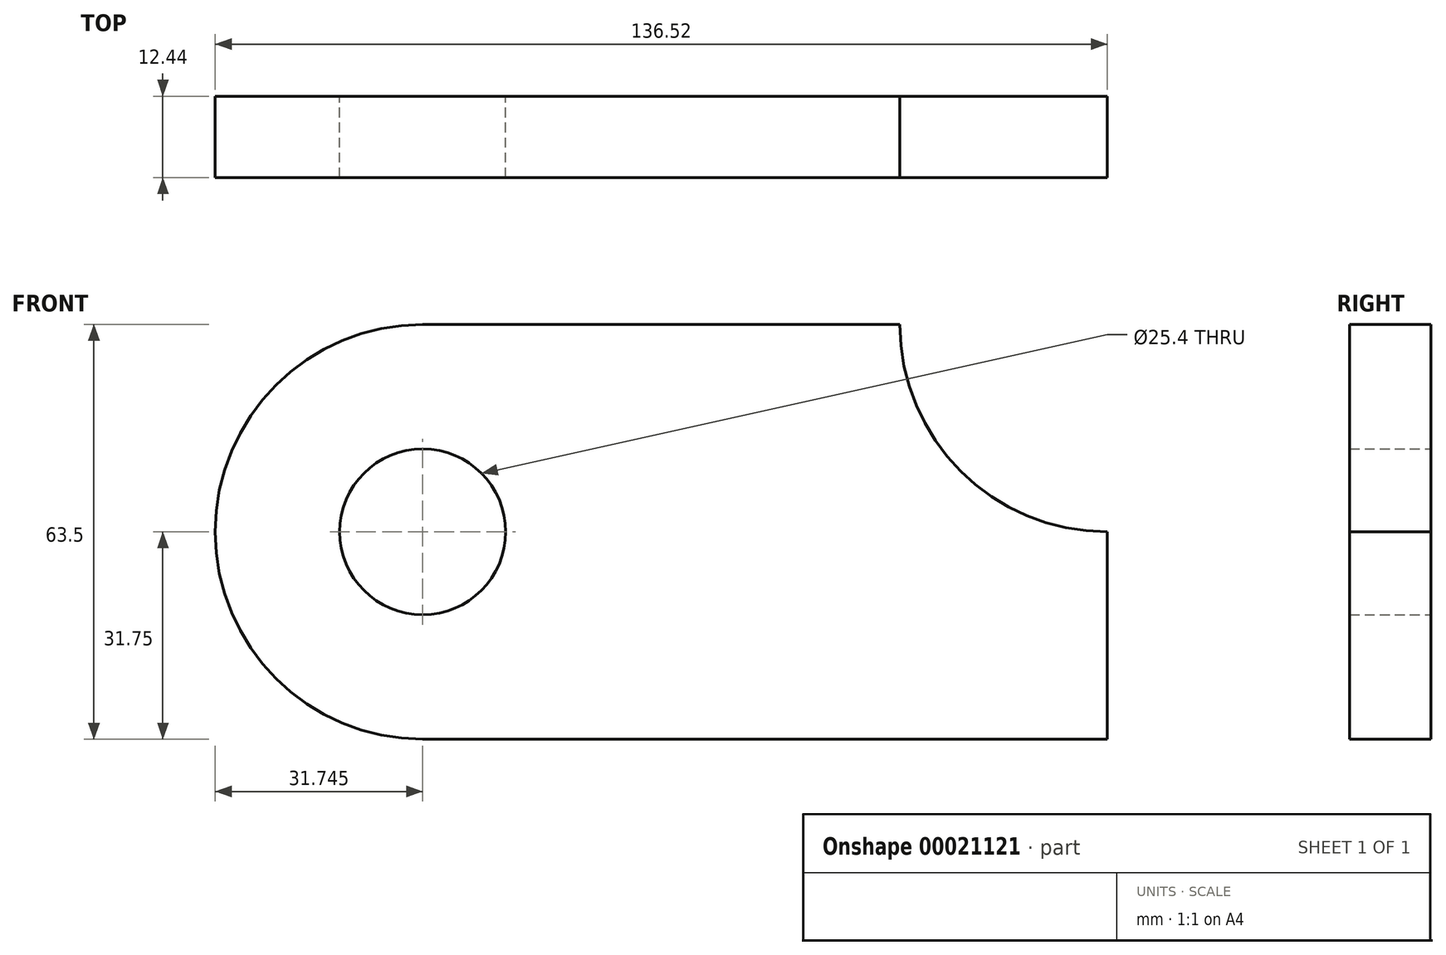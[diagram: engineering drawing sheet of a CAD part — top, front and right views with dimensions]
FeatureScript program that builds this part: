
annotation { "Feature Type Name" : "Feature", "Feature Type Description" : "" }
export const myFeature = defineFeature(function(context is Context, id is Id, definition is map)
    precondition{}
    {
        {
            var Q0;
            Q0=qCreatedBy(makeId("Front.planeOp"),FACE);
            var sketch = newSketch(context, id + "F0", { "sketchPlane" : qUnion([Q0])});
            skLineSegment(sketch, "E0.bottom", {"start": v(0, 0) * mm, "end": v(-104.78, 0) * mm});
            skLineSegment(sketch, "E0.top", {"start": v(0, 63.5) * mm, "end": v(-104.77, 63.5) * mm});
            skLineSegment(sketch, "E0.left", {"start": v(0, 0) * mm, "end": v(0, 63.5) * mm});
            skLineSegment(sketch, "E0.right", {"start": v(-104.78, 0) * mm, "end": v(-104.77, 63.5) * mm});
            skCircle(sketch, "E1", {"center": v(-104.77, 31.75) * mm, "radius": 31.75 * mm});
            skCircle(sketch, "E2", {"center": v(-104.77, 31.75) * mm, "radius": 12.7 * mm});
            skCircle(sketch, "E3", {"center": v(0, 63.5) * mm, "radius": 31.75 * mm});
            skSolve(sketch);
        }
        {
            var Q0;
            {var subQ4=sQuery(id+"F0.wireOp",EDGE,"E0.bottom");Q0=makeQuery(id+"F0.imprint","IMPRINT",FACE,{"disambiguationData":[TD([[makeQuery(id+"F0.imprint","IMPRINT",EDGE,{"derivedFrom":subQ4}),-1.0]])]});}
            var Q1;
            {var subQ0=sQuery(id+"F0.wireOp",EDGE,"E2");var subQ1=sQuery(id+"F0.wireOp",EDGE,"E0.right");var subQ3=makeQuery(id+"F0.imprint","INTERSECT",VERTEX,{"disambiguationData":[OD(0.0)],"derivedFrom":[subQ1,subQ0]});Q1=makeQuery(id+"F0.imprint","IMPRINT",FACE,{"disambiguationData":[TD([[makeQuery(id+"F0.imprint","IMPRINT",EDGE,{"disambiguationData":[TD([[subQ3,1.0]])],"derivedFrom":subQ0}),-1.0]])]});}
            var Q2;
            {var subQ0=sQuery(id+"F0.wireOp",EDGE,"E2");var subQ1=sQuery(id+"F0.wireOp",EDGE,"E0.right");var subQ3=makeQuery(id+"F0.imprint","INTERSECT",VERTEX,{"disambiguationData":[OD(0.0)],"derivedFrom":[subQ1,subQ0]});Q2=makeQuery(id+"F0.imprint","IMPRINT",FACE,{"disambiguationData":[TD([[makeQuery(id+"F0.imprint","IMPRINT",EDGE,{"disambiguationData":[TD([[subQ3,-1.0]])],"derivedFrom":subQ0}),-1.0]])]});}
            extrude(context, id + "F1", {"entities" : qUnion([Q0, Q1, Q2]), "depth" : 12.44 * mm});
        }
    });
